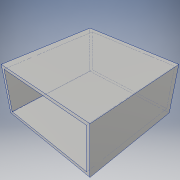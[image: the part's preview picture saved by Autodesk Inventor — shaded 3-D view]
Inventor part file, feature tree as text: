
AUTODESK INVENTOR PART (.ipt)
format: ipt  version: 2019 (Build 230136000, 136)  size: 102,400 bytes
history: native  units: in
note: dims shown in document units (in); Inventor stores cm internally (conversion verified against a paired STEP export)
features: extrude x1, sketch x1
ambient origin geometry x8: Origin, YZ Plane, XZ Plane, XY Plane, X Axis, Y Axis, Z Axis, Center Point
bodies: Solid1 (feature_tree)
feature tree (2):
  extrude  "Extrusion1"  Depth=0.125in
  sketch  "Sketch1"  dims[d0=2.0in d1=0.125in d2=4.0in d3=0.0in d11=4.0in d12=0.125in]
